# Revit family: Sink-Wall_Mount-Utility-KOHLER-Bannon-K-6719
name_source: partatom
category: Plumbing Fixtures
revit_build: Autodesk Revit 2015 (Build: 20140606_1530(x64)
units: mm (PartAtom-declared; Revit-internal decimal feet)

## types (1)
- 0-White
    ADA Compliant = No
    Assembly Code = D2010400
    CW Connection = No
    Cold Water Inlet = Cold Water Inlet
    Date Modified = 09/19/2019
    Default Elevation = 36"
    Description = 24 Inch x 20-1/4 Inch wall-mounted or P-trap mounted service sink with rim guard and blank back
    Drain Included = No
    Finish = KOHLER-Cast_Iron-0-White
    HW Connection = No
    Height = 23"
    Hot Water Inlet = Hot Water Inlet
    Length = 24"
    Manufacturer = KOHLER Co.
    MasterFormat 1995 = 15410
    MasterFormat 2004 = 22.41.16
    Material = Cast Iron
    Model = K-6719-0
    Product Documentation Link = https://www.us.kohler.com
    Product Name = Bannon
    Product Page URL = http://www.us.kohler.com
    URL = https://www.us.kohler.com
    Vent Connection = No
    Waste Connection = Yes
    Waste Water Outlet = Waste Water Outlet
    WaterSense Certified = No
    Width = 20 1/4"

## geometry (parser evidence)
native form markers: Sweep x5
no freeform markers — native parametric forms only
